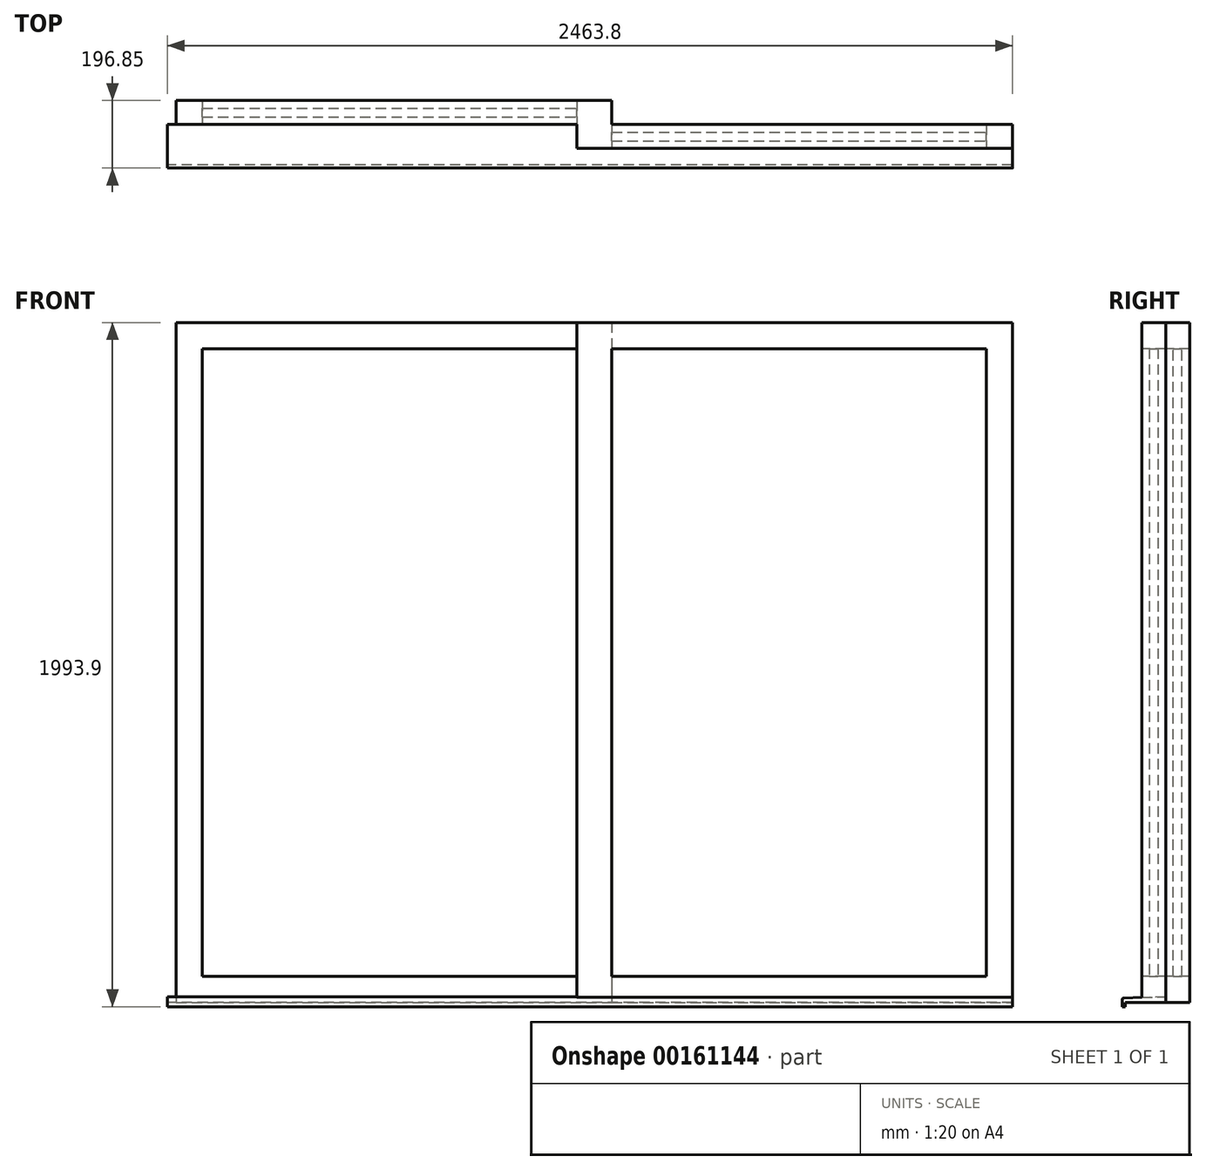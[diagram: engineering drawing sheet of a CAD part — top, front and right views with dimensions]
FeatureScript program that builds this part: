
annotation { "Feature Type Name" : "Feature", "Feature Type Description" : "" }
export const myFeature = defineFeature(function(context is Context, id is Id, definition is map)
    precondition{}
    {
        {
            var Q0;
            Q0=qCreatedBy(makeId("Top.planeOp"),FACE);
            var sketch = newSketch(context, id + "F0", { "sketchPlane" : qUnion([Q0])});
            skLineSegment(sketch, "E0.bottom", {"start": v(0, 0) * mm, "end": v(1168.4, 0) * mm});
            skLineSegment(sketch, "E0.top", {"start": v(0, 69.85) * mm, "end": v(1270, 69.85) * mm});
            skLineSegment(sketch, "E0.left", {"start": v(0, 0) * mm, "end": v(0, 69.85) * mm});
            skLineSegment(sketch, "E0.right", {"start": v(1270, 0) * mm, "end": v(1270, 69.85) * mm});
            skLineSegment(sketch, "E1.bottom", {"start": v(1270, 0) * mm, "end": v(2438.4, 0) * mm});
            skLineSegment(sketch, "E1.top", {"start": v(1168.4, -69.85) * mm, "end": v(2438.4, -69.85) * mm});
            skLineSegment(sketch, "E1.left", {"start": v(1168.4, 0) * mm, "end": v(1168.4, -69.85) * mm});
            skLineSegment(sketch, "E1.right", {"start": v(2438.4, 0) * mm, "end": v(2438.4, -69.85) * mm});
            skPoint(sketch, "E2.orphan", {"position": v(1168.4, 69.85) * mm});
            skSolve(sketch);
        }
        {
            var Q0;
            Q0=qSketchRegion(id+"F0",true);
            extrude(context, id + "F1", {"entities" : qUnion([Q0]), "depth" : 1981.2 * mm});
        }
        {
            var Q0;
            Q0=makeQuery(id+"F1.opExtrude","SWEPT_FACE",FACE,{"disambiguationData":[OSD([sQuery(id+"F0.wireOp",EDGE,"E0.bottom")])]});
            var sketch = newSketch(context, id + "F2", { "sketchPlane" : qUnion([Q0])});
            skLineSegment(sketch, "E3.bottom", {"start": v(76.2, 1905) * mm, "end": v(1168.4, 1905) * mm});
            skLineSegment(sketch, "E3.top", {"start": v(76.2, 76.2) * mm, "end": v(1168.4, 76.2) * mm});
            skLineSegment(sketch, "E3.left", {"start": v(76.2, 1905) * mm, "end": v(76.2, 76.2) * mm});
            skLineSegment(sketch, "E3.right", {"start": v(1168.4, 1905) * mm, "end": v(1168.4, 76.2) * mm});
            skLineSegment(sketch, "E4.bottom", {"start": v(1270, 1905) * mm, "end": v(2362.2, 1905) * mm});
            skLineSegment(sketch, "E4.top", {"start": v(1270, 76.2) * mm, "end": v(2362.2, 76.2) * mm});
            skLineSegment(sketch, "E4.left", {"start": v(1270, 1905) * mm, "end": v(1270, 76.2) * mm});
            skLineSegment(sketch, "E4.right", {"start": v(2362.2, 1905) * mm, "end": v(2362.2, 76.2) * mm});
            skSolve(sketch);
        }
        {
            var Q0;
            Q0=qSketchRegion(id+"F2",true);
            extrude(context, id + "F3", {"entities" : qUnion([Q0]), "oppositeDirection" : true, "depth" : 76.2 * mm, "hasSecondDirection" : true, "secondDirectionOppositeDirection" : false, "secondDirectionDepth" : 76.2 * mm});
        }
        {
            var Q0;
            Q0=makeQuery(id+"F3.opExtrude","SWEPT_BODY",BODY,{"disambiguationData":[OSD([sQuery(id+"F2.wireOp",EDGE,"E3.bottom"),sQuery(id+"F2.wireOp",EDGE,"E3.top"),sQuery(id+"F2.wireOp",EDGE,"E3.left"),sQuery(id+"F2.wireOp",EDGE,"E3.right")])]});
            var Q1;
            Q1=makeQuery(id+"F3.opExtrude","SWEPT_BODY",BODY,{"disambiguationData":[OSD([sQuery(id+"F2.wireOp",EDGE,"E4.bottom"),sQuery(id+"F2.wireOp",EDGE,"E4.top"),sQuery(id+"F2.wireOp",EDGE,"E4.left"),sQuery(id+"F2.wireOp",EDGE,"E4.right")])]});
            var Q2;
            Q2=makeQuery(id+"F1.opExtrude","SWEPT_BODY",BODY,{"disambiguationData":[OSD([sQuery(id+"F0.wireOp",EDGE,"E0.bottom"),sQuery(id+"F0.wireOp",EDGE,"E0.top"),sQuery(id+"F0.wireOp",EDGE,"E0.left"),sQuery(id+"F0.wireOp",EDGE,"E0.right"),sQuery(id+"F0.wireOp",EDGE,"E1.bottom"),sQuery(id+"F0.wireOp",EDGE,"E1.top"),sQuery(id+"F0.wireOp",EDGE,"E1.left"),sQuery(id+"F0.wireOp",EDGE,"E1.right")])]});
            booleanBodies(context, id + "F4", {"operationType" : BooleanOperationType.SUBTRACTION, "tools" : qUnion([Q0, Q1]), "targets" : qUnion([Q2])});
        }
        {
            var Q0;
            Q0=qCreatedBy(makeId("Front.planeOp"),FACE);
            cPlane(context, id + "F5", {"entities" : qUnion([Q0]), "cplaneType" : CPlaneType.OFFSET, "offset" : 34.92 * mm, "oppositeDirection" : true, "width" : 152.4 * mm, "height" : 152.4 * mm});
        }
        {
            var Q0;
            Q0=qCreatedBy(id+"F5.planeOp",FACE);
            var sketch = newSketch(context, id + "F6", { "sketchPlane" : qUnion([Q0])});
            skLineSegment(sketch, "E5.bottom", {"start": v(76.2, 76.2) * mm, "end": v(1168.4, 76.2) * mm});
            skLineSegment(sketch, "E5.top", {"start": v(76.2, 1905) * mm, "end": v(1168.4, 1905) * mm});
            skLineSegment(sketch, "E5.left", {"start": v(76.2, 76.2) * mm, "end": v(76.2, 1905) * mm});
            skLineSegment(sketch, "E5.right", {"start": v(1168.4, 76.2) * mm, "end": v(1168.4, 1905) * mm});
            skSolve(sketch);
        }
        {
            var Q0;
            Q0=qSketchRegion(id+"F6",true);
            extrude(context, id + "F7", {"entities" : qUnion([Q0]), "endBound" : BoundingType.SYMMETRIC, "depth" : 25.4 * mm});
        }
        {
            var Q0;
            Q0=qCreatedBy(makeId("Front.planeOp"),FACE);
            cPlane(context, id + "F8", {"entities" : qUnion([Q0]), "cplaneType" : CPlaneType.OFFSET, "offset" : 34.92 * mm, "width" : 152.4 * mm, "height" : 152.4 * mm});
        }
        {
            var Q0;
            Q0=qCreatedBy(id+"F8.planeOp",FACE);
            var sketch = newSketch(context, id + "F9", { "sketchPlane" : qUnion([Q0])});
            skLineSegment(sketch, "E6.bottom", {"start": v(1270, 1905) * mm, "end": v(2362.2, 1905) * mm});
            skLineSegment(sketch, "E6.top", {"start": v(1270, 76.2) * mm, "end": v(2362.2, 76.2) * mm});
            skLineSegment(sketch, "E6.left", {"start": v(1270, 1905) * mm, "end": v(1270, 76.2) * mm});
            skLineSegment(sketch, "E6.right", {"start": v(2362.2, 1905) * mm, "end": v(2362.2, 76.2) * mm});
            skSolve(sketch);
        }
        {
            var Q0;
            Q0=qSketchRegion(id+"F9",true);
            extrude(context, id + "F10", {"entities" : qUnion([Q0]), "endBound" : BoundingType.SYMMETRIC, "depth" : 25.4 * mm});
        }
        {
            var Q0;
            Q0=makeQuery(id+"F1.opExtrude","SWEPT_FACE",FACE,{"disambiguationData":[OSD([sQuery(id+"F0.wireOp",EDGE,"E0.left")])]});
            var sketch = newSketch(context, id + "F11", { "sketchPlane" : qUnion([Q0])});
            skLineSegment(sketch, "E7", {"start": v(0, 0) * mm, "end": v(0, 15.88) * mm});
            skLineSegment(sketch, "E8", {"start": v(127, 12.7) * mm, "end": v(127, -12.7) * mm});
            skLineSegment(sketch, "E9", {"start": v(127, -12.7) * mm, "end": v(117.48, -12.7) * mm});
            skLineSegment(sketch, "E10", {"start": v(117.48, -12.7) * mm, "end": v(117.48, 0) * mm});
            skLineSegment(sketch, "E11", {"start": v(117.48, 0) * mm, "end": v(0, 0) * mm});
            skPoint(sketch, "E12.orphan", {"position": v(127, 0) * mm});
            skLineSegment(sketch, "E13", {"start": v(0, 15.88) * mm, "end": v(127, 12.7) * mm});
            skSolve(sketch);
        }
        {
            var Q0;
            Q0=qSketchRegion(id+"F11",true);
            extrude(context, id + "F12", {"entities" : qUnion([Q0]), "operationType" : NewBodyOperationType.ADD, "oppositeDirection" : true, "depth" : 2438.4 * mm, "hasSecondDirection" : true, "secondDirectionOppositeDirection" : false, "secondDirectionDepth" : 25.4 * mm});
        }
        {
            var Q0;
            Q0=makeQuery(id+"F12.opExtrude","SWEPT_EDGE",EDGE,{"disambiguationData":[OSD([sQuery(id+"F11.wireOp",EDGE,"E8"),sQuery(id+"F11.wireOp",EDGE,"E13")])]});
            fillet(context, id + "F13", {"entities" : qUnion([Q0]), "radius" : 5.08 * mm, "tangentPropagation" : true, "allowEdgeOverflow" : false});
        }
    });
